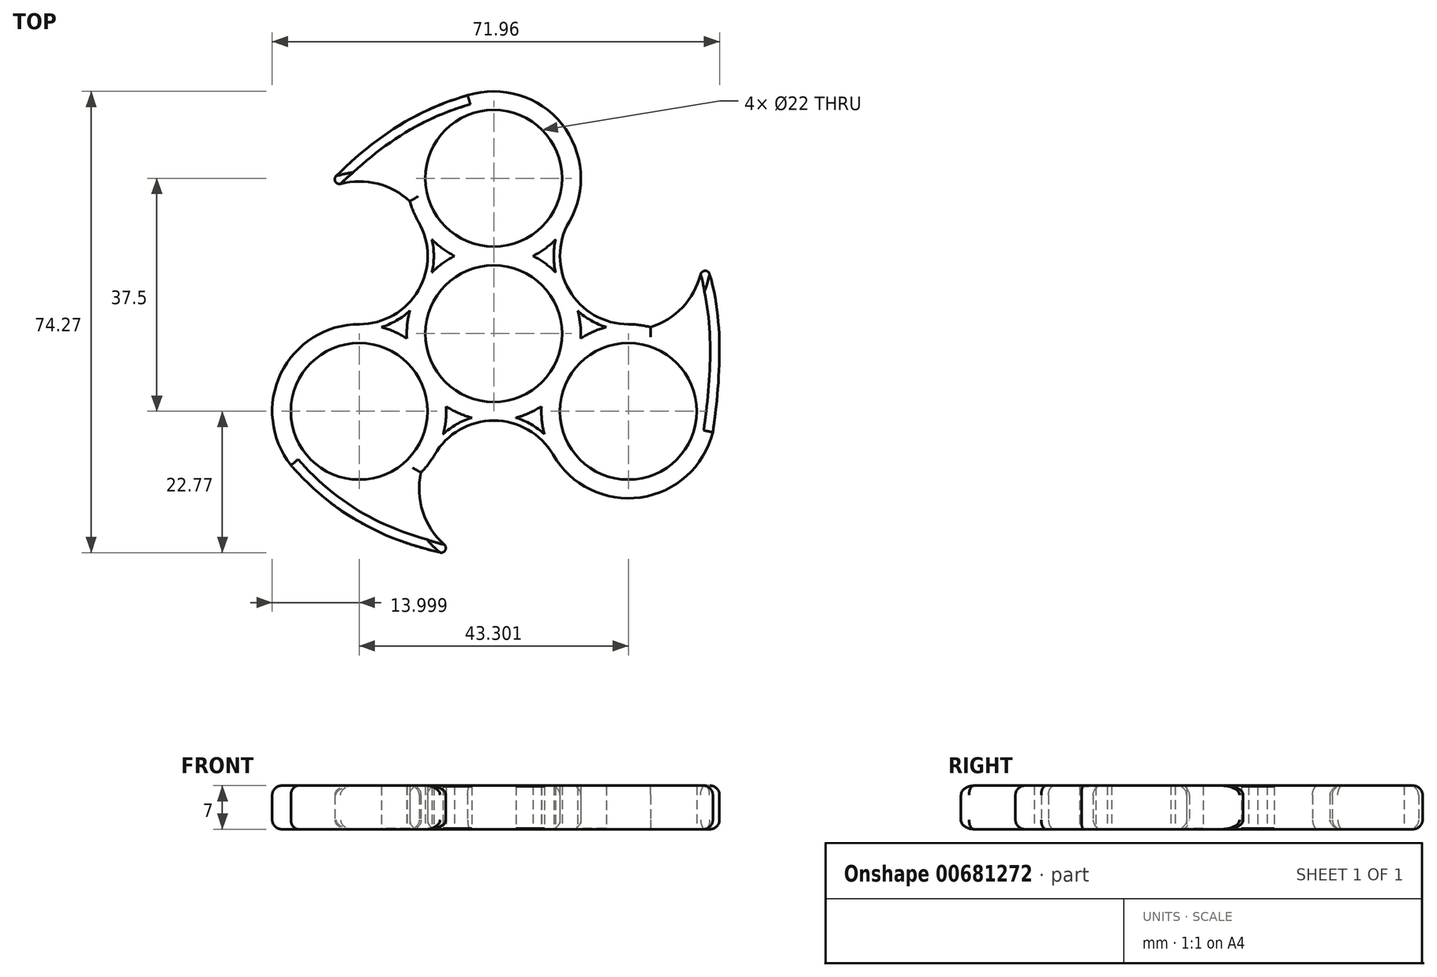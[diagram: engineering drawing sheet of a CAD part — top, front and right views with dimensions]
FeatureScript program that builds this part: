
annotation { "Feature Type Name" : "Feature", "Feature Type Description" : "" }
export const myFeature = defineFeature(function(context is Context, id is Id, definition is map)
    precondition{}
    {
        {
            var Q0;
            Q0=qCreatedBy(makeId("Top.planeOp"),FACE);
            var sketch = newSketch(context, id + "F0", { "sketchPlane" : qUnion([Q0])});
            skCircle(sketch, "E0", {"center": v(0, 0) * mm, "radius": 11 * mm});
            skCircle(sketch, "E1", {"center": v(-21.65, 12.5) * mm, "radius": 11 * mm});
            skCircle(sketch, "E2", {"center": v(21.65, 12.5) * mm, "radius": 11 * mm});
            skCircle(sketch, "E3", {"center": v(0, 25) * mm, "radius": 11 * mm});
            skCircle(sketch, "E4", {"center": v(0, -25) * mm, "radius": 11 * mm});
            skCircle(sketch, "E5", {"center": v(21.65, -12.5) * mm, "radius": 11 * mm});
            skCircle(sketch, "E6", {"center": v(-21.65, -12.5) * mm, "radius": 11 * mm});
            skCircle(sketch, "E7.0", {"center": v(0, 0) * mm, "radius": 14 * mm});
            skCircle(sketch, "E8.0", {"center": v(0, 25) * mm, "radius": 14 * mm});
            skCircle(sketch, "E9.0", {"center": v(21.65, -12.5) * mm, "radius": 14 * mm});
            skCircle(sketch, "E10.0", {"center": v(-21.65, -12.5) * mm, "radius": 14 * mm});
            skCircle(sketch, "E11.0", {"center": v(-21.65, 12.5) * mm, "radius": 12 * mm});
            skCircle(sketch, "E12.0", {"center": v(21.65, 12.5) * mm, "radius": 12 * mm});
            skCircle(sketch, "E13.0", {"center": v(0, -25) * mm, "radius": 12 * mm});
            skCircle(sketch, "E14.0", {"center": v(-50.48, 43.37) * mm, "radius": 12 * mm});
            skFitSpline(sketch, "E15", {"points": [v(-32.64, -21.18) * mm, v(-4.63, -36.07) * mm], "startDerivative": vector(23.75, -27.5) * mm, "endDerivative": vector(31.85, -5.63) * mm});
            skFitSpline(sketch, "E16", {"points": [v(35.24, -15.87) * mm, v(33.65, 12.6) * mm], "startDerivative": vector(4.86, 33.85) * mm, "endDerivative": vector(-9.62, 23.12) * mm});
            skFitSpline(sketch, "E17", {"points": [v(-4.2, 38.35) * mm, v(-27.86, 22.77) * mm], "startDerivative": vector(-28.69, -8.04) * mm, "endDerivative": vector(-20.09, -21.85) * mm});
            skSolve(sketch);
        }
        {
            var Q0;
            {var subQ0=sQuery(id+"F0.wireOp",EDGE,"E11.0");var subQ1=sQuery(id+"F0.wireOp",EDGE,"E8.0");var subQ2=makeQuery(id+"F0.imprint","INTERSECT",VERTEX,{"disambiguationData":[OD(0.0)],"derivedFrom":[subQ1,subQ0]});Q0=makeQuery(id+"F0.imprint","IMPRINT",FACE,{"disambiguationData":[TD([[makeQuery(id+"F0.imprint","IMPRINT",EDGE,{"disambiguationData":[TD([[subQ2,-1.0]])],"derivedFrom":subQ1}),1.0]])]});}
            var Q1;
            {var subQ0=sQuery(id+"F0.wireOp",EDGE,"E8.0");var subQ1=makeQuery(id+"F0.imprint","INTERSECT",VERTEX,{"derivedFrom":[sQuery(id+"F0.wireOp",EDGE,"E2"),subQ0]});Q1=makeQuery(id+"F0.imprint","IMPRINT",FACE,{"disambiguationData":[TD([[makeQuery(id+"F0.imprint","IMPRINT",EDGE,{"disambiguationData":[TD([[subQ1,1.0]])],"derivedFrom":subQ0}),1.0]])]});}
            var Q2;
            {var subQ0=sQuery(id+"F0.wireOp",EDGE,"E12.0");var subQ1=sQuery(id+"F0.wireOp",EDGE,"E9.0");var subQ2=makeQuery(id+"F0.imprint","INTERSECT",VERTEX,{"disambiguationData":[OD(0.0)],"derivedFrom":[subQ1,subQ0]});Q2=makeQuery(id+"F0.imprint","IMPRINT",FACE,{"disambiguationData":[TD([[makeQuery(id+"F0.imprint","IMPRINT",EDGE,{"disambiguationData":[TD([[subQ2,-1.0]])],"derivedFrom":subQ1}),1.0]])]});}
            var Q3;
            {var subQ0=sQuery(id+"F0.wireOp",EDGE,"E9.0");var subQ1=makeQuery(id+"F0.imprint","INTERSECT",VERTEX,{"derivedFrom":[sQuery(id+"F0.wireOp",EDGE,"E4"),subQ0]});Q3=makeQuery(id+"F0.imprint","IMPRINT",FACE,{"disambiguationData":[TD([[makeQuery(id+"F0.imprint","IMPRINT",EDGE,{"disambiguationData":[TD([[subQ1,1.0]])],"derivedFrom":subQ0}),1.0]])]});}
            var Q4;
            {var subQ0=sQuery(id+"F0.wireOp",EDGE,"E10.0");var subQ1=makeQuery(id+"F0.imprint","INTERSECT",VERTEX,{"derivedFrom":[sQuery(id+"F0.wireOp",EDGE,"E1"),subQ0]});Q4=makeQuery(id+"F0.imprint","IMPRINT",FACE,{"disambiguationData":[TD([[makeQuery(id+"F0.imprint","IMPRINT",EDGE,{"disambiguationData":[TD([[subQ1,1.0]])],"derivedFrom":subQ0}),1.0]])]});}
            var Q5;
            {var subQ0=sQuery(id+"F0.wireOp",EDGE,"E13.0");var subQ1=sQuery(id+"F0.wireOp",EDGE,"E10.0");var subQ2=makeQuery(id+"F0.imprint","INTERSECT",VERTEX,{"disambiguationData":[OD(0.0)],"derivedFrom":[subQ1,subQ0]});Q5=makeQuery(id+"F0.imprint","IMPRINT",FACE,{"disambiguationData":[TD([[makeQuery(id+"F0.imprint","IMPRINT",EDGE,{"disambiguationData":[TD([[subQ2,-1.0]])],"derivedFrom":subQ1}),1.0]])]});}
            var Q6;
            {var subQ5=sQuery(id+"F0.wireOp",EDGE,"E3");Q6=makeQuery(id+"F0.imprint","IMPRINT",FACE,{"disambiguationData":[TD([[makeQuery(id+"F0.imprint","IMPRINT",EDGE,{"derivedFrom":subQ5}),-1.0]])]});}
            var Q7;
            {var subQ5=sQuery(id+"F0.wireOp",EDGE,"E5");Q7=makeQuery(id+"F0.imprint","IMPRINT",FACE,{"disambiguationData":[TD([[makeQuery(id+"F0.imprint","IMPRINT",EDGE,{"derivedFrom":subQ5}),-1.0]])]});}
            var Q8;
            {var subQ5=sQuery(id+"F0.wireOp",EDGE,"E6");Q8=makeQuery(id+"F0.imprint","IMPRINT",FACE,{"disambiguationData":[TD([[makeQuery(id+"F0.imprint","IMPRINT",EDGE,{"derivedFrom":subQ5}),-1.0]])]});}
            var Q9;
            {var subQ0=sQuery(id+"F0.wireOp",EDGE,"E7.0");var subQ1=sQuery(id+"F0.wireOp",EDGE,"E4");var subQ2=makeQuery(id+"F0.imprint","INTERSECT",VERTEX,{"derivedFrom":[subQ1,subQ0]});Q9=makeQuery(id+"F0.imprint","IMPRINT",FACE,{"disambiguationData":[TD([[makeQuery(id+"F0.imprint","IMPRINT",EDGE,{"disambiguationData":[TD([[subQ2,-1.0]])],"derivedFrom":subQ1}),-1.0]])]});}
            var Q10;
            {var subQ0=sQuery(id+"F0.wireOp",EDGE,"E7.0");var subQ1=makeQuery(id+"F0.imprint","INTERSECT",VERTEX,{"derivedFrom":[sQuery(id+"F0.wireOp",EDGE,"E4"),subQ0]});Q10=makeQuery(id+"F0.imprint","IMPRINT",FACE,{"disambiguationData":[TD([[makeQuery(id+"F0.imprint","IMPRINT",EDGE,{"disambiguationData":[TD([[subQ1,1.0]])],"derivedFrom":subQ0}),1.0]])]});}
            var Q11;
            {var subQ0=sQuery(id+"F0.wireOp",EDGE,"E7.0");var subQ1=sQuery(id+"F0.wireOp",EDGE,"E4");var subQ2=makeQuery(id+"F0.imprint","INTERSECT",VERTEX,{"derivedFrom":[subQ1,subQ0]});Q11=makeQuery(id+"F0.imprint","IMPRINT",FACE,{"disambiguationData":[TD([[makeQuery(id+"F0.imprint","IMPRINT",EDGE,{"disambiguationData":[TD([[subQ2,1.0]])],"derivedFrom":subQ1}),-1.0]])]});}
            var Q12;
            {var subQ5=sQuery(id+"F0.wireOp",EDGE,"E10.0");var subQ6=sQuery(id+"F0.wireOp",EDGE,"E0");var subQ7=makeQuery(id+"F0.imprint","INTERSECT",VERTEX,{"derivedFrom":[subQ6,subQ5]});Q12=makeQuery(id+"F0.imprint","IMPRINT",FACE,{"disambiguationData":[TD([[makeQuery(id+"F0.imprint","IMPRINT",EDGE,{"disambiguationData":[TD([[subQ7,-1.0]])],"derivedFrom":subQ6}),-1.0]])]});}
            var Q13;
            {var subQ0=sQuery(id+"F0.wireOp",EDGE,"E7.0");var subQ1=makeQuery(id+"F0.imprint","INTERSECT",VERTEX,{"derivedFrom":[sQuery(id+"F0.wireOp",EDGE,"E5"),subQ0]});Q13=makeQuery(id+"F0.imprint","IMPRINT",FACE,{"disambiguationData":[TD([[makeQuery(id+"F0.imprint","IMPRINT",EDGE,{"disambiguationData":[TD([[subQ1,1.0]])],"derivedFrom":subQ0}),1.0]])]});}
            var Q14;
            {var subQ0=sQuery(id+"F0.wireOp",EDGE,"E8.0");var subQ1=sQuery(id+"F0.wireOp",EDGE,"E0");var subQ2=makeQuery(id+"F0.imprint","INTERSECT",VERTEX,{"derivedFrom":[subQ1,subQ0]});Q14=makeQuery(id+"F0.imprint","IMPRINT",FACE,{"disambiguationData":[TD([[makeQuery(id+"F0.imprint","IMPRINT",EDGE,{"disambiguationData":[TD([[subQ2,1.0]])],"derivedFrom":subQ1}),-1.0]])]});}
            var Q15;
            {var subQ0=sQuery(id+"F0.wireOp",EDGE,"E7.0");var subQ1=makeQuery(id+"F0.imprint","INTERSECT",VERTEX,{"derivedFrom":[sQuery(id+"F0.wireOp",EDGE,"E2"),subQ0]});Q15=makeQuery(id+"F0.imprint","IMPRINT",FACE,{"disambiguationData":[TD([[makeQuery(id+"F0.imprint","IMPRINT",EDGE,{"disambiguationData":[TD([[subQ1,1.0]])],"derivedFrom":subQ0}),1.0]])]});}
            var Q16;
            {var subQ0=sQuery(id+"F0.wireOp",EDGE,"E7.0");var subQ1=sQuery(id+"F0.wireOp",EDGE,"E2");var subQ2=makeQuery(id+"F0.imprint","INTERSECT",VERTEX,{"derivedFrom":[subQ1,subQ0]});Q16=makeQuery(id+"F0.imprint","IMPRINT",FACE,{"disambiguationData":[TD([[makeQuery(id+"F0.imprint","IMPRINT",EDGE,{"disambiguationData":[TD([[subQ2,1.0]])],"derivedFrom":subQ1}),-1.0]])]});}
            var Q17;
            {var subQ0=sQuery(id+"F0.wireOp",EDGE,"E7.0");var subQ1=sQuery(id+"F0.wireOp",EDGE,"E2");var subQ2=makeQuery(id+"F0.imprint","INTERSECT",VERTEX,{"derivedFrom":[subQ1,subQ0]});Q17=makeQuery(id+"F0.imprint","IMPRINT",FACE,{"disambiguationData":[TD([[makeQuery(id+"F0.imprint","IMPRINT",EDGE,{"disambiguationData":[TD([[subQ2,-1.0]])],"derivedFrom":subQ1}),-1.0]])]});}
            var Q18;
            {var subQ0=sQuery(id+"F0.wireOp",EDGE,"E7.0");var subQ1=makeQuery(id+"F0.imprint","INTERSECT",VERTEX,{"derivedFrom":[sQuery(id+"F0.wireOp",EDGE,"E3"),subQ0]});Q18=makeQuery(id+"F0.imprint","IMPRINT",FACE,{"disambiguationData":[TD([[makeQuery(id+"F0.imprint","IMPRINT",EDGE,{"disambiguationData":[TD([[subQ1,1.0]])],"derivedFrom":subQ0}),1.0]])]});}
            var Q19;
            {var subQ0=sQuery(id+"F0.wireOp",EDGE,"E8.0");var subQ1=sQuery(id+"F0.wireOp",EDGE,"E1");var subQ2=makeQuery(id+"F0.imprint","INTERSECT",VERTEX,{"derivedFrom":[subQ1,subQ0]});Q19=makeQuery(id+"F0.imprint","IMPRINT",FACE,{"disambiguationData":[TD([[makeQuery(id+"F0.imprint","IMPRINT",EDGE,{"disambiguationData":[TD([[subQ2,1.0]])],"derivedFrom":subQ1}),-1.0]])]});}
            var Q20;
            {var subQ0=sQuery(id+"F0.wireOp",EDGE,"E10.0");var subQ1=sQuery(id+"F0.wireOp",EDGE,"E1");var subQ2=makeQuery(id+"F0.imprint","INTERSECT",VERTEX,{"derivedFrom":[subQ1,subQ0]});Q20=makeQuery(id+"F0.imprint","IMPRINT",FACE,{"disambiguationData":[TD([[makeQuery(id+"F0.imprint","IMPRINT",EDGE,{"disambiguationData":[TD([[subQ2,-1.0]])],"derivedFrom":subQ1}),-1.0]])]});}
            var Q21;
            {var subQ0=sQuery(id+"F0.wireOp",EDGE,"E7.0");var subQ1=makeQuery(id+"F0.imprint","INTERSECT",VERTEX,{"derivedFrom":[sQuery(id+"F0.wireOp",EDGE,"E1"),subQ0]});Q21=makeQuery(id+"F0.imprint","IMPRINT",FACE,{"disambiguationData":[TD([[makeQuery(id+"F0.imprint","IMPRINT",EDGE,{"disambiguationData":[TD([[subQ1,1.0]])],"derivedFrom":subQ0}),1.0]])]});}
            var Q22;
            {var subQ1=sQuery(id+"F0.wireOp",EDGE,"E0");var subQ7=sQuery(id+"F0.wireOp",EDGE,"E10.0");var subQ10=makeQuery(id+"F0.imprint","INTERSECT",VERTEX,{"derivedFrom":[subQ1,subQ7]});Q22=makeQuery(id+"F0.imprint","IMPRINT",FACE,{"disambiguationData":[TD([[makeQuery(id+"F0.imprint","IMPRINT",EDGE,{"disambiguationData":[TD([[subQ10,1.0]])],"derivedFrom":subQ1}),-1.0]])]});}
            var Q23;
            {var subQ0=sQuery(id+"F0.wireOp",EDGE,"E7.0");var subQ1=makeQuery(id+"F0.imprint","INTERSECT",VERTEX,{"derivedFrom":[sQuery(id+"F0.wireOp",EDGE,"E6"),subQ0]});Q23=makeQuery(id+"F0.imprint","IMPRINT",FACE,{"disambiguationData":[TD([[makeQuery(id+"F0.imprint","IMPRINT",EDGE,{"disambiguationData":[TD([[subQ1,1.0]])],"derivedFrom":subQ0}),1.0]])]});}
            var Q24;
            {var subQ0=sQuery(id+"F0.wireOp",EDGE,"E17");Q24=makeQuery(id+"F0.imprint","IMPRINT",FACE,{"disambiguationData":[TD([[makeQuery(id+"F0.imprint","IMPRINT",EDGE,{"derivedFrom":subQ0}),1.0]])]});}
            var Q25;
            {var subQ0=sQuery(id+"F0.wireOp",EDGE,"E16");var subQ1=sQuery(id+"F0.wireOp",EDGE,"E9.0");var subQ2=makeQuery(id+"F0.imprint","INTERSECT",VERTEX,{"disambiguationData":[OD(1.0)],"derivedFrom":[subQ1,subQ0]});Q25=makeQuery(id+"F0.imprint","IMPRINT",FACE,{"disambiguationData":[TD([[makeQuery(id+"F0.imprint","IMPRINT",EDGE,{"disambiguationData":[TD([[subQ2,-1.0]])],"derivedFrom":subQ1}),-1.0]])]});}
            var Q26;
            {var subQ0=sQuery(id+"F0.wireOp",EDGE,"E15");var subQ1=sQuery(id+"F0.wireOp",EDGE,"E10.0");var subQ2=makeQuery(id+"F0.imprint","INTERSECT",VERTEX,{"disambiguationData":[OD(1.0)],"derivedFrom":[subQ1,subQ0]});Q26=makeQuery(id+"F0.imprint","IMPRINT",FACE,{"disambiguationData":[TD([[makeQuery(id+"F0.imprint","IMPRINT",EDGE,{"disambiguationData":[TD([[subQ2,-1.0]])],"derivedFrom":subQ1}),-1.0]])]});}
            extrude(context, id + "F1", {"entities" : qUnion([Q0, Q1, Q2, Q3, Q4, Q5, Q6, Q7, Q8, Q9, Q10, Q11, Q12, Q13, Q14, Q15, Q16, Q17, Q18, Q19, Q20, Q21, Q22, Q23, Q24, Q25, Q26]), "depth" : 7 * mm, "offsetDistance" : 25 * mm});
        }
        {
            var Q0;
            Q0=makeQuery(id+"F1.opExtrude","CAP_EDGE",EDGE,{"disambiguationData":[OSD([sQuery(id+"F0.wireOp",EDGE,"E17")])],"isStart":false});
            var Q1;
            {var subQ0=sQuery(id+"F0.wireOp",EDGE,"E8.0");var subQ1=makeQuery(id+"F0.imprint","INTERSECT",VERTEX,{"disambiguationData":[OD(0.0)],"derivedFrom":[subQ0,sQuery(id+"F0.wireOp",EDGE,"E12.0")]});Q1=makeQuery(id+"F1.opExtrude","CAP_EDGE",EDGE,{"disambiguationData":[OSD([subQ0]),TDD([makeQuery(id+"F0.imprint","IMPRINT",EDGE,{"disambiguationData":[TD([[subQ1,1.0]])],"derivedFrom":subQ0}),makeQuery(id+"F0.imprint","IMPRINT",EDGE,{"disambiguationData":[TD([[makeQuery(id+"F0.imprint","INTERSECT",VERTEX,{"derivedFrom":[subQ0,sQuery(id+"F0.wireOp",EDGE,"E17")]}),1.0]])],"derivedFrom":subQ0})])],"isStart":false});}
            var Q2;
            Q2=makeQuery(id+"F1.opExtrude","CAP_EDGE",EDGE,{"disambiguationData":[OSD([sQuery(id+"F0.wireOp",EDGE,"E2")])],"isStart":false});
            var Q3;
            {var subQ0=sQuery(id+"F0.wireOp",EDGE,"E12.0");Q3=makeQuery(id+"F1.opExtrude","CAP_EDGE",EDGE,{"disambiguationData":[OSD([subQ0]),TDD([makeQuery(id+"F0.imprint","IMPRINT",EDGE,{"disambiguationData":[TD([[makeQuery(id+"F0.imprint","INTERSECT",VERTEX,{"derivedFrom":[subQ0,sQuery(id+"F0.wireOp",EDGE,"E16")]}),1.0]])],"derivedFrom":subQ0})])],"isStart":false});}
            var Q4;
            {var subQ0=sQuery(id+"F0.wireOp",EDGE,"E9.0");Q4=makeQuery(id+"F1.opExtrude","CAP_EDGE",EDGE,{"disambiguationData":[OSD([subQ0]),TDD([makeQuery(id+"F0.imprint","IMPRINT",EDGE,{"disambiguationData":[TD([[makeQuery(id+"F0.imprint","INTERSECT",VERTEX,{"derivedFrom":[sQuery(id+"F0.wireOp",EDGE,"E2"),subQ0]}),1.0]])],"derivedFrom":subQ0})])],"isStart":false});}
            var Q5;
            Q5=makeQuery(id+"F1.opExtrude","CAP_EDGE",EDGE,{"disambiguationData":[OSD([sQuery(id+"F0.wireOp",EDGE,"E16")])],"isStart":false});
            var Q6;
            {var subQ0=sQuery(id+"F0.wireOp",EDGE,"E9.0");var subQ1=makeQuery(id+"F0.imprint","INTERSECT",VERTEX,{"disambiguationData":[OD(0.0)],"derivedFrom":[subQ0,sQuery(id+"F0.wireOp",EDGE,"E13.0")]});Q6=makeQuery(id+"F1.opExtrude","CAP_EDGE",EDGE,{"disambiguationData":[OSD([subQ0]),TDD([makeQuery(id+"F0.imprint","IMPRINT",EDGE,{"disambiguationData":[TD([[subQ1,1.0]])],"derivedFrom":subQ0}),makeQuery(id+"F0.imprint","IMPRINT",EDGE,{"disambiguationData":[TD([[makeQuery(id+"F0.imprint","INTERSECT",VERTEX,{"disambiguationData":[OD(0.0)],"derivedFrom":[subQ0,sQuery(id+"F0.wireOp",EDGE,"E16")]}),1.0]])],"derivedFrom":subQ0})])],"isStart":false});}
            var Q7;
            Q7=makeQuery(id+"F1.opExtrude","CAP_EDGE",EDGE,{"disambiguationData":[OSD([sQuery(id+"F0.wireOp",EDGE,"E4")])],"isStart":false});
            var Q8;
            {var subQ0=sQuery(id+"F0.wireOp",EDGE,"E13.0");Q8=makeQuery(id+"F1.opExtrude","CAP_EDGE",EDGE,{"disambiguationData":[OSD([subQ0]),TDD([makeQuery(id+"F0.imprint","IMPRINT",EDGE,{"disambiguationData":[TD([[makeQuery(id+"F0.imprint","INTERSECT",VERTEX,{"derivedFrom":[subQ0,sQuery(id+"F0.wireOp",EDGE,"E15")]}),1.0]])],"derivedFrom":subQ0})])],"isStart":false});}
            var Q9;
            {var subQ0=sQuery(id+"F0.wireOp",EDGE,"E10.0");Q9=makeQuery(id+"F1.opExtrude","CAP_EDGE",EDGE,{"disambiguationData":[OSD([subQ0]),TDD([makeQuery(id+"F0.imprint","IMPRINT",EDGE,{"disambiguationData":[TD([[makeQuery(id+"F0.imprint","INTERSECT",VERTEX,{"derivedFrom":[sQuery(id+"F0.wireOp",EDGE,"E4"),subQ0]}),1.0]])],"derivedFrom":subQ0})])],"isStart":false});}
            var Q10;
            Q10=makeQuery(id+"F1.opExtrude","CAP_EDGE",EDGE,{"disambiguationData":[OSD([sQuery(id+"F0.wireOp",EDGE,"E15")])],"isStart":false});
            var Q11;
            {var subQ0=sQuery(id+"F0.wireOp",EDGE,"E10.0");var subQ1=makeQuery(id+"F0.imprint","INTERSECT",VERTEX,{"disambiguationData":[OD(0.0)],"derivedFrom":[subQ0,sQuery(id+"F0.wireOp",EDGE,"E11.0")]});Q11=makeQuery(id+"F1.opExtrude","CAP_EDGE",EDGE,{"disambiguationData":[OSD([subQ0]),TDD([makeQuery(id+"F0.imprint","IMPRINT",EDGE,{"disambiguationData":[TD([[subQ1,1.0]])],"derivedFrom":subQ0}),makeQuery(id+"F0.imprint","IMPRINT",EDGE,{"disambiguationData":[TD([[makeQuery(id+"F0.imprint","INTERSECT",VERTEX,{"disambiguationData":[OD(0.0)],"derivedFrom":[subQ0,sQuery(id+"F0.wireOp",EDGE,"E15")]}),1.0]])],"derivedFrom":subQ0})])],"isStart":false});}
            var Q12;
            Q12=makeQuery(id+"F1.opExtrude","CAP_EDGE",EDGE,{"disambiguationData":[OSD([sQuery(id+"F0.wireOp",EDGE,"E1")])],"isStart":false});
            var Q13;
            {var subQ0=sQuery(id+"F0.wireOp",EDGE,"E8.0");Q13=makeQuery(id+"F1.opExtrude","CAP_EDGE",EDGE,{"disambiguationData":[OSD([subQ0]),TDD([makeQuery(id+"F0.imprint","IMPRINT",EDGE,{"disambiguationData":[TD([[makeQuery(id+"F0.imprint","INTERSECT",VERTEX,{"derivedFrom":[sQuery(id+"F0.wireOp",EDGE,"E1"),subQ0]}),1.0]])],"derivedFrom":subQ0})])],"isStart":false});}
            var Q14;
            {var subQ0=sQuery(id+"F0.wireOp",EDGE,"E11.0");Q14=makeQuery(id+"F1.opExtrude","CAP_EDGE",EDGE,{"disambiguationData":[OSD([subQ0]),TDD([makeQuery(id+"F0.imprint","IMPRINT",EDGE,{"disambiguationData":[TD([[makeQuery(id+"F0.imprint","INTERSECT",VERTEX,{"derivedFrom":[subQ0,sQuery(id+"F0.wireOp",EDGE,"E17")]}),1.0]])],"derivedFrom":subQ0})])],"isStart":false});}
            var Q15;
            Q15=makeQuery(id+"F1.opExtrude","CAP_EDGE",EDGE,{"disambiguationData":[OSD([sQuery(id+"F0.wireOp",EDGE,"E16")])],"isStart":true});
            var Q16;
            {var subQ0=sQuery(id+"F0.wireOp",EDGE,"E9.0");var subQ1=makeQuery(id+"F0.imprint","INTERSECT",VERTEX,{"disambiguationData":[OD(0.0)],"derivedFrom":[subQ0,sQuery(id+"F0.wireOp",EDGE,"E13.0")]});Q16=makeQuery(id+"F1.opExtrude","CAP_EDGE",EDGE,{"disambiguationData":[OSD([subQ0]),TDD([makeQuery(id+"F0.imprint","IMPRINT",EDGE,{"disambiguationData":[TD([[subQ1,1.0]])],"derivedFrom":subQ0}),makeQuery(id+"F0.imprint","IMPRINT",EDGE,{"disambiguationData":[TD([[makeQuery(id+"F0.imprint","INTERSECT",VERTEX,{"disambiguationData":[OD(0.0)],"derivedFrom":[subQ0,sQuery(id+"F0.wireOp",EDGE,"E16")]}),1.0]])],"derivedFrom":subQ0})])],"isStart":true});}
            var Q17;
            Q17=makeQuery(id+"F1.opExtrude","CAP_EDGE",EDGE,{"disambiguationData":[OSD([sQuery(id+"F0.wireOp",EDGE,"E4")])],"isStart":true});
            var Q18;
            {var subQ0=sQuery(id+"F0.wireOp",EDGE,"E13.0");Q18=makeQuery(id+"F1.opExtrude","CAP_EDGE",EDGE,{"disambiguationData":[OSD([subQ0]),TDD([makeQuery(id+"F0.imprint","IMPRINT",EDGE,{"disambiguationData":[TD([[makeQuery(id+"F0.imprint","INTERSECT",VERTEX,{"derivedFrom":[subQ0,sQuery(id+"F0.wireOp",EDGE,"E15")]}),1.0]])],"derivedFrom":subQ0})])],"isStart":true});}
            var Q19;
            Q19=makeQuery(id+"F1.opExtrude","CAP_EDGE",EDGE,{"disambiguationData":[OSD([sQuery(id+"F0.wireOp",EDGE,"E15")])],"isStart":true});
            var Q20;
            {var subQ0=sQuery(id+"F0.wireOp",EDGE,"E10.0");var subQ1=makeQuery(id+"F0.imprint","INTERSECT",VERTEX,{"disambiguationData":[OD(0.0)],"derivedFrom":[subQ0,sQuery(id+"F0.wireOp",EDGE,"E11.0")]});Q20=makeQuery(id+"F1.opExtrude","CAP_EDGE",EDGE,{"disambiguationData":[OSD([subQ0]),TDD([makeQuery(id+"F0.imprint","IMPRINT",EDGE,{"disambiguationData":[TD([[subQ1,1.0]])],"derivedFrom":subQ0}),makeQuery(id+"F0.imprint","IMPRINT",EDGE,{"disambiguationData":[TD([[makeQuery(id+"F0.imprint","INTERSECT",VERTEX,{"disambiguationData":[OD(0.0)],"derivedFrom":[subQ0,sQuery(id+"F0.wireOp",EDGE,"E15")]}),1.0]])],"derivedFrom":subQ0})])],"isStart":true});}
            var Q21;
            Q21=makeQuery(id+"F1.opExtrude","CAP_EDGE",EDGE,{"disambiguationData":[OSD([sQuery(id+"F0.wireOp",EDGE,"E1")])],"isStart":true});
            var Q22;
            {var subQ0=sQuery(id+"F0.wireOp",EDGE,"E11.0");Q22=makeQuery(id+"F1.opExtrude","CAP_EDGE",EDGE,{"disambiguationData":[OSD([subQ0]),TDD([makeQuery(id+"F0.imprint","IMPRINT",EDGE,{"disambiguationData":[TD([[makeQuery(id+"F0.imprint","INTERSECT",VERTEX,{"derivedFrom":[subQ0,sQuery(id+"F0.wireOp",EDGE,"E17")]}),1.0]])],"derivedFrom":subQ0})])],"isStart":true});}
            var Q23;
            Q23=makeQuery(id+"F1.opExtrude","CAP_EDGE",EDGE,{"disambiguationData":[OSD([sQuery(id+"F0.wireOp",EDGE,"E17")])],"isStart":true});
            var Q24;
            {var subQ0=sQuery(id+"F0.wireOp",EDGE,"E8.0");var subQ1=makeQuery(id+"F0.imprint","INTERSECT",VERTEX,{"disambiguationData":[OD(0.0)],"derivedFrom":[subQ0,sQuery(id+"F0.wireOp",EDGE,"E12.0")]});Q24=makeQuery(id+"F1.opExtrude","CAP_EDGE",EDGE,{"disambiguationData":[OSD([subQ0]),TDD([makeQuery(id+"F0.imprint","IMPRINT",EDGE,{"disambiguationData":[TD([[subQ1,1.0]])],"derivedFrom":subQ0}),makeQuery(id+"F0.imprint","IMPRINT",EDGE,{"disambiguationData":[TD([[makeQuery(id+"F0.imprint","INTERSECT",VERTEX,{"derivedFrom":[subQ0,sQuery(id+"F0.wireOp",EDGE,"E17")]}),1.0]])],"derivedFrom":subQ0})])],"isStart":true});}
            var Q25;
            Q25=makeQuery(id+"F1.opExtrude","CAP_EDGE",EDGE,{"disambiguationData":[OSD([sQuery(id+"F0.wireOp",EDGE,"E2")])],"isStart":true});
            var Q26;
            {var subQ0=sQuery(id+"F0.wireOp",EDGE,"E9.0");Q26=makeQuery(id+"F1.opExtrude","CAP_EDGE",EDGE,{"disambiguationData":[OSD([subQ0]),TDD([makeQuery(id+"F0.imprint","IMPRINT",EDGE,{"disambiguationData":[TD([[makeQuery(id+"F0.imprint","INTERSECT",VERTEX,{"derivedFrom":[sQuery(id+"F0.wireOp",EDGE,"E2"),subQ0]}),1.0]])],"derivedFrom":subQ0})])],"isStart":true});}
            var Q27;
            {var subQ0=sQuery(id+"F0.wireOp",EDGE,"E12.0");Q27=makeQuery(id+"F1.opExtrude","CAP_EDGE",EDGE,{"disambiguationData":[OSD([subQ0]),TDD([makeQuery(id+"F0.imprint","IMPRINT",EDGE,{"disambiguationData":[TD([[makeQuery(id+"F0.imprint","INTERSECT",VERTEX,{"derivedFrom":[subQ0,sQuery(id+"F0.wireOp",EDGE,"E16")]}),1.0]])],"derivedFrom":subQ0})])],"isStart":true});}
            fillet(context, id + "F2", {"entities" : qUnion([Q0, Q1, Q2, Q3, Q4, Q5, Q6, Q7, Q8, Q9, Q10, Q11, Q12, Q13, Q14, Q15, Q16, Q17, Q18, Q19, Q20, Q21, Q22, Q23, Q24, Q25, Q26, Q27]), "radius" : 1.5 * mm, "tangentPropagation" : true, "allowEdgeOverflow" : false});
        }
        {
            var Q0;
            Q0=makeQuery(id+"F1.opExtrude","SWEPT_EDGE",EDGE,{"disambiguationData":[OSD([sQuery(id+"F0.wireOp",EDGE,"E11.0"),sQuery(id+"F0.wireOp",EDGE,"E17")])]});
            var Q1;
            Q1=makeQuery(id+"F1.opExtrude","SWEPT_EDGE",EDGE,{"disambiguationData":[OSD([sQuery(id+"F0.wireOp",EDGE,"E12.0"),sQuery(id+"F0.wireOp",EDGE,"E16")])]});
            var Q2;
            Q2=makeQuery(id+"F1.opExtrude","SWEPT_EDGE",EDGE,{"disambiguationData":[OSD([sQuery(id+"F0.wireOp",EDGE,"E13.0"),sQuery(id+"F0.wireOp",EDGE,"E15")])]});
            fillet(context, id + "F3", {"entities" : qUnion([Q0, Q1, Q2]), "radius" : 0.74 * mm, "tangentPropagation" : true, "allowEdgeOverflow" : false});
        }
    });
